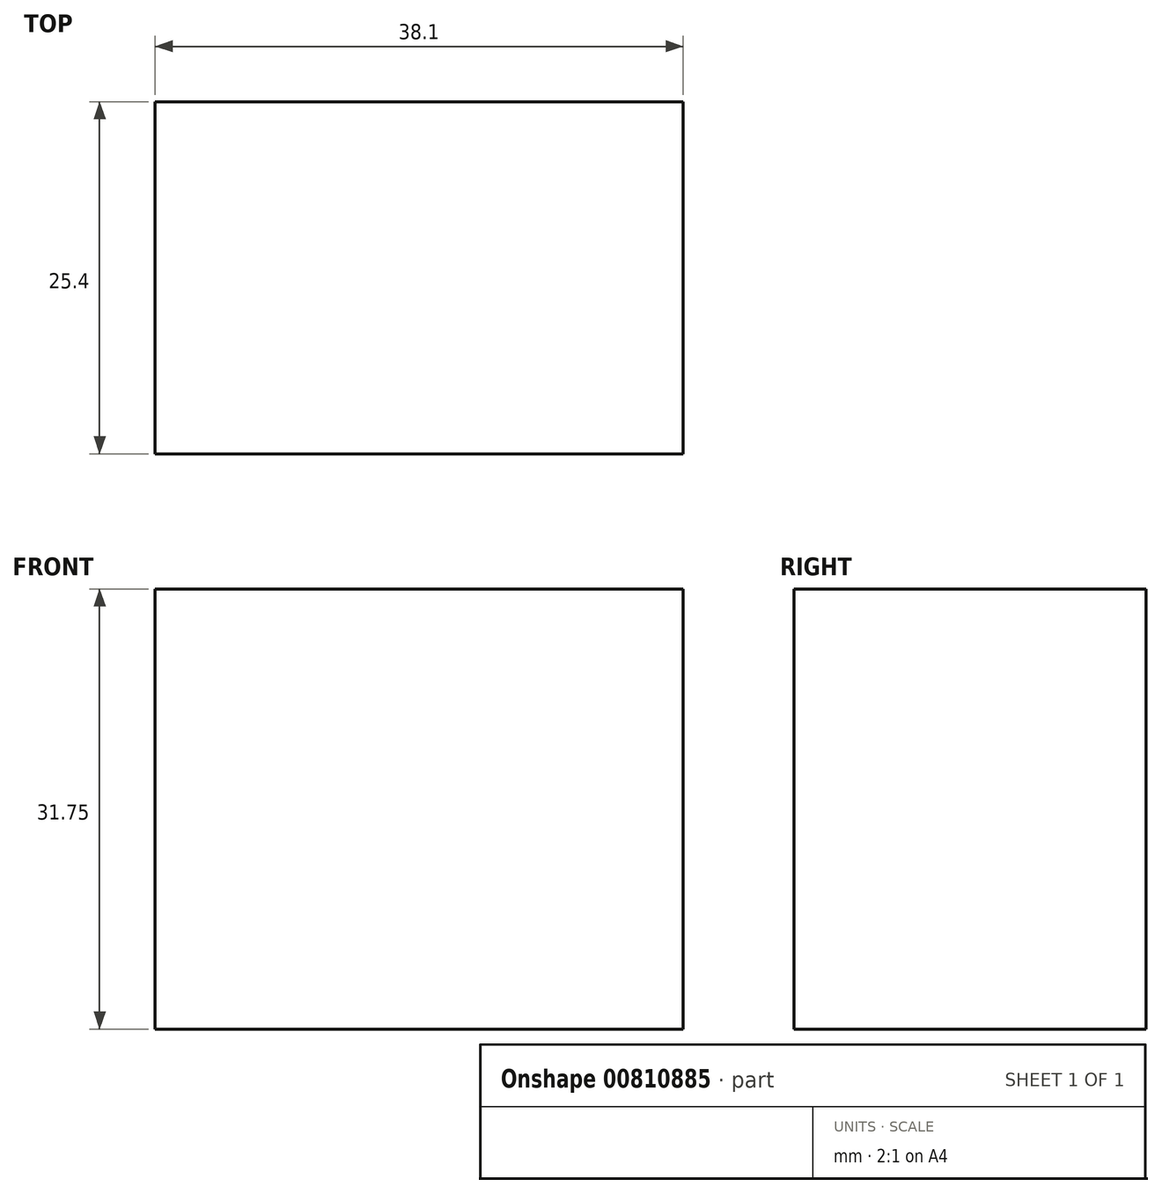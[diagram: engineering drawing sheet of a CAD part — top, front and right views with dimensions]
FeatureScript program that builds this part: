
annotation { "Feature Type Name" : "Feature", "Feature Type Description" : "" }
export const myFeature = defineFeature(function(context is Context, id is Id, definition is map)
    precondition{}
    {
        {
            var Q0;
            Q0=qCreatedBy(makeId("Front.planeOp"),FACE);
            var sketch = newSketch(context, id + "F0", { "sketchPlane" : qUnion([Q0])});
            skLineSegment(sketch, "E0", {"start": v(0, 0) * mm, "end": v(38.1, 0) * mm});
            skLineSegment(sketch, "E1", {"start": v(0, 0) * mm, "end": v(0, 31.75) * mm});
            skLineSegment(sketch, "E2", {"start": v(0, 31.75) * mm, "end": v(38.1, 31.75) * mm});
            skLineSegment(sketch, "E3", {"start": v(38.1, 31.75) * mm, "end": v(38.1, 0) * mm});
            skSolve(sketch);
        }
        {
            var Q0;
            Q0=makeQuery(id+"F0.imprint","IMPRINT",FACE,{"disambiguationData":[TD([[makeQuery(id+"F0.imprint","IMPRINT",EDGE,{"derivedFrom":sQuery(id+"F0.wireOp",EDGE,"E0")}),1.0]])]});
            extrude(context, id + "F1", {"entities" : qUnion([Q0]), "depth" : 25.4 * mm, "offsetDistance" : 25.4 * mm});
        }
    });
